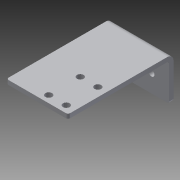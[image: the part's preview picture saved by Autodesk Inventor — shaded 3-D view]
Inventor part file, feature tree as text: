
AUTODESK INVENTOR PART (.ipt)
format: ipt  version: 2014 (Build 180170000, 170)  size: 130,560 bytes
history: native  units: in
note: dims shown in document units (in); Inventor stores cm internally (conversion verified against a paired STEP export)
features: sheet_metal_op x4, sketch x3, other x2, fillet x1, extrude x1
ambient origin geometry x8: Origin, YZ Plane, XZ Plane, XY Plane, X Axis, Y Axis, Z Axis, Center Point
bodies: Solid1 (feature_tree)
feature tree (11):
  sheet_metal_op  "Face1"
  sheet_metal_op  "Flange1"
  fillet  "Fillet1"  Radius=1.75in
  extrude  "Extrusion1"  Depth=0.163in
  sketch  "Sketch1"  dims[d1=1.0in d2=0.163in]
  other  "Plate1"
  sketch  "Sketch2"  dims[d4=0.7874in d6=1.0in d7=0.3937in d9=1.0in]
  other  "Plate2"
  sheet_metal_op  "Bend1"
  sheet_metal_op  "Corner1"
  sketch  "Sketch3"  dims[d11=0.125in d12=0.125in d13=0.0625in d14=0.25in d15=0.125in d16=3.0in d17=90.0deg d18=0.05in d19=0.5in d20=0.125in d21=0.125in d22=0.0625in d23=1.35in d24=0.75in d25=1.5in d27=0.19in d28=0.125in d29=0.2265in d30=1.0in d31=0.0in d34=0.25in d35=0.875in]
